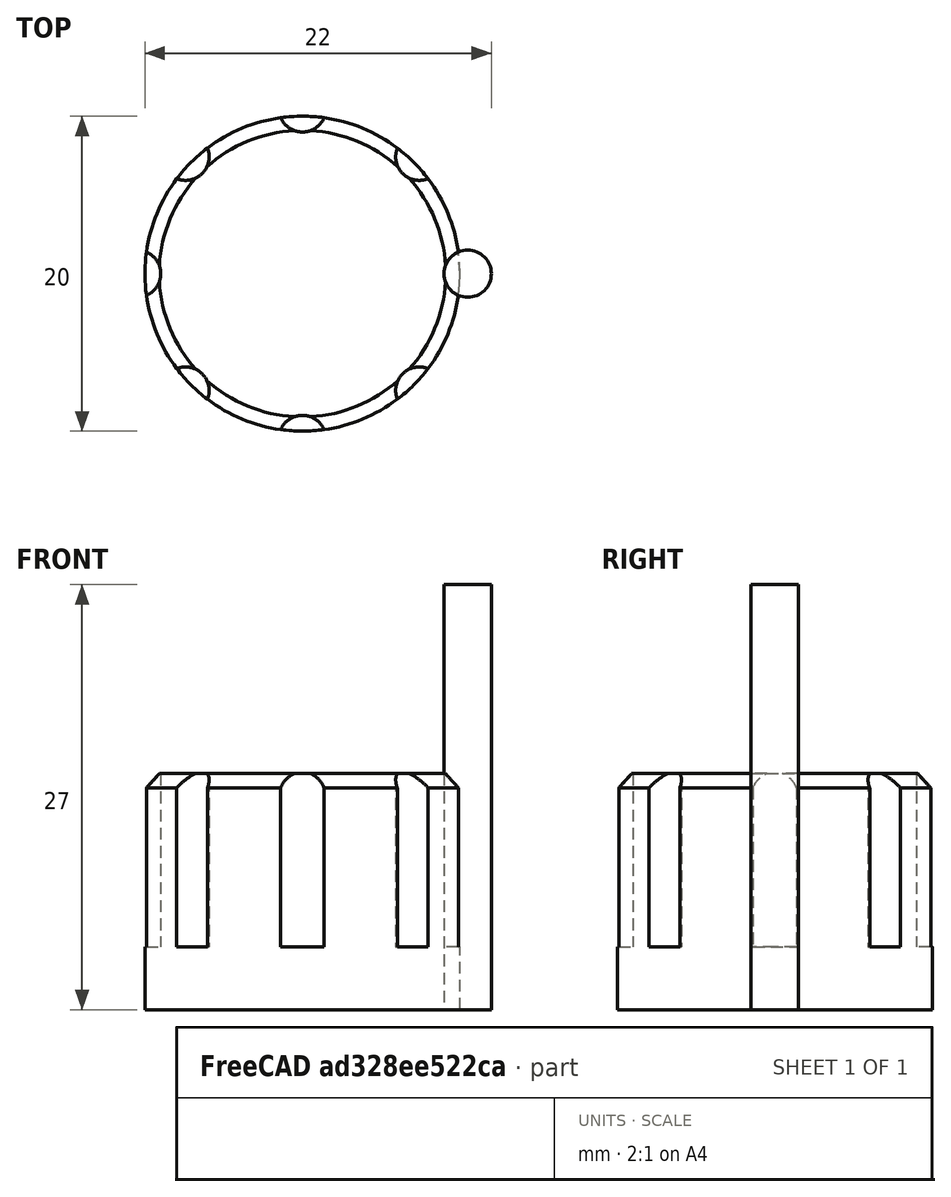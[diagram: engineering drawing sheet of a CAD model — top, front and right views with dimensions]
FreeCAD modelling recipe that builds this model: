
FCSTD DOCUMENT  (FreeCAD 1.0R39319 (Git))
Label: ojt1_t12r01_buttom_potenciometer
License: All rights reserved
LicenseURL: https://en.wikipedia.org/wiki/All_rights_reserved
objects: Part::Cylinder×2, Part::FeaturePython×1, Part::Cut×1, Part::Chamfer×1
note: 4 computed .brp shape members not serialized (recipe doc carries the construction recipe); baked Part::Feature solids carry a one-line shape summary decoded from their .brp

FEATURE [Part::Cylinder] Cylinder002
  Angle = 360
  AttacherType = Attacher::AttachEngine3D
  FirstAngle = 0
  Height = 15
  Radius = 10
  SecondAngle = 0
FEATURE [Part::Cylinder] Cylinder003
  Angle = 360
  AttacherType = Attacher::AttachEngine3D
  FirstAngle = 0
  Height = 27
  Placement = pos=(10.5,0,0) rot=(0,0,1;0rad)
  Radius = 1.5
  SecondAngle = 0
FEATURE [Part::FeaturePython] Array001  # Draft array (typed FeaturePython)
  AlwaysSyncPlacement = false
  Angle = 360
  ArrayType = 1
  Axis = (0,0,0)
  Base = -> Cylinder003
  Center = (0,0,0)
  Count = 8
  ExpandArray = false
  Fuse = false
  IntervalAxis = (0,0,0)
  IntervalX = (50,0,0)
  IntervalY = (0,50,0)
  IntervalZ = (0,0,50)
  NumberCircles = 3
  NumberPolar = 8
  NumberX = 2
  NumberY = 2
  NumberZ = 1
  Placement = pos=(0,0,4) rot=(0,0,1;0rad)
  PlacementList = 8 placements: [(10.5,0,0),(7.42462,7.42462,0),(0,10.5,0),(-7.42462,7.42462,0),(-10.5,1.28588e-15,0),(-7.42462,-7.42462,0),(-2.33147e-15,-10.5,0),(7.42462,-7.42462,0)]
  RadialDistance = 50
  ScaleList = (8) [(1,1,1),(1,1,1),(1,1,1),(1,1,1),(1,1,1),(1,1,1),(1,1,1),(1,1,1)]
  Symmetry = 1
  TangentialDistance = 25
FEATURE [Part::Cut] Cut
  Base = -> Cylinder002
  Refine = true
  Tool = -> Array001
FEATURE [Part::Chamfer] Chamfer
  Base = -> Cut
  EdgeLinks = -> Cut [Edge5,Edge9,Edge13,Edge17,Edge21,Edge25,Edge29,Edge33]
  Edges = 8 edges r=0.9: [Edge5,Edge9,Edge13,Edge17,Edge21,Edge25,Edge29,Edge33]
